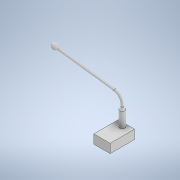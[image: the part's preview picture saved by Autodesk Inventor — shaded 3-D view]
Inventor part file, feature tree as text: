
AUTODESK INVENTOR PART (.ipt)
format: ipt  version: 2021 (Build 250183000, 183)  size: 162,816 bytes
history: native  units: mm
features: other x8, sketch x8, extrude x3, projected_geometry x3, sweep x1
ambient origin geometry x8: Origin, YZ Plane, XZ Plane, XY Plane, X Axis, Y Axis, Z Axis, Center Point
bodies: Body1 (feature_tree), Body2 (feature_tree), Body3 (feature_tree)
feature tree (23):
  other  "實體1"
  extrude  "擠出1"  Depth=100.0mm
  extrude  "擠出2"  Depth=150.0mm
  extrude  "擠出3"  Depth=55.0mm TaperAngle=0.0deg
  sweep  "掃掠1"
  other  "迴轉1"
  sketch  "草圖1"
  sketch  "草圖2"
  sketch  "草圖3"
  projected_geometry  "投影迴路1"
  sketch  "草圖4"
  sketch  "草圖5"
  sketch  "草圖6"
  projected_geometry  "投影迴路2"
  other  "Srf1"
  sketch  "草圖7"
  projected_geometry  "投影迴路3"
  sketch  "草圖8"
  other  "Srf2"
  other  "擠出表面2"
  other  "擠出表面1"
  other  "投影切割邊1"
  other  "投影切割邊2"
